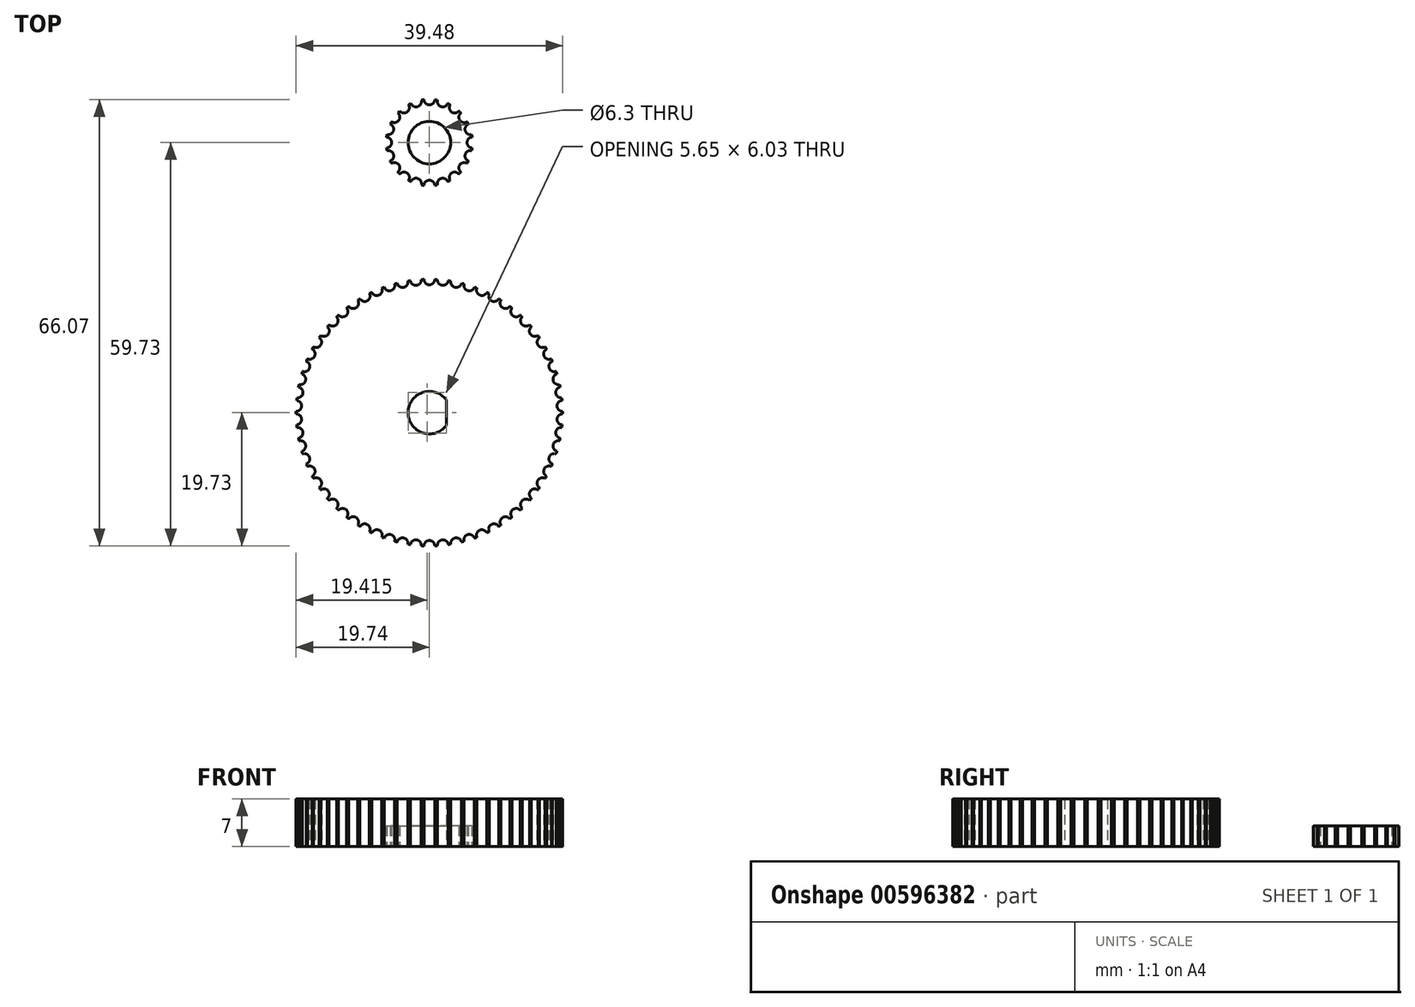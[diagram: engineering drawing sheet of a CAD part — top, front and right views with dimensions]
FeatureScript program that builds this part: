
annotation { "Feature Type Name" : "Feature", "Feature Type Description" : "" }
export const myFeature = defineFeature(function(context is Context, id is Id, definition is map)
    precondition{}
    {
        {
            var Q0;
            Q0=qCreatedBy(makeId("Top.planeOp"),FACE);
            var sketch = newSketch(context, id + "F0", { "sketchPlane" : qUnion([Q0])});
            skCircle(sketch, "E0", {"center": v(0, 0) * mm, "radius": 6.4 * mm});
            skCircle(sketch, "E1", {"center": v(0, 6.4) * mm, "radius": 0.8 * mm});
            skCircle(sketch, "E2.1.0", {"center": v(-1.98, 6.08) * mm, "radius": 0.8 * mm});
            skCircle(sketch, "E2.2.0", {"center": v(-3.76, 5.17) * mm, "radius": 0.8 * mm});
            skCircle(sketch, "E3.1.3.0", {"center": v(-5.17, 3.76) * mm, "radius": 0.8 * mm});
            skCircle(sketch, "E3.1.4.0", {"center": v(-6.08, 1.98) * mm, "radius": 0.8 * mm});
            skCircle(sketch, "E3.1.5.0", {"center": v(-6.4, 0) * mm, "radius": 0.8 * mm});
            skCircle(sketch, "E3.1.6.0", {"center": v(-6.08, -1.98) * mm, "radius": 0.8 * mm});
            skCircle(sketch, "E3.1.7.0", {"center": v(-5.17, -3.76) * mm, "radius": 0.8 * mm});
            skCircle(sketch, "E3.1.8.0", {"center": v(-3.76, -5.17) * mm, "radius": 0.8 * mm});
            skCircle(sketch, "E3.1.9.0", {"center": v(-1.98, -6.08) * mm, "radius": 0.8 * mm});
            skCircle(sketch, "E3.1.10.0", {"center": v(0, -6.4) * mm, "radius": 0.8 * mm});
            skCircle(sketch, "E3.1.11.0", {"center": v(1.98, -6.08) * mm, "radius": 0.8 * mm});
            skCircle(sketch, "E3.1.12.0", {"center": v(3.76, -5.17) * mm, "radius": 0.8 * mm});
            skCircle(sketch, "E3.1.13.0", {"center": v(5.17, -3.76) * mm, "radius": 0.8 * mm});
            skCircle(sketch, "E3.1.14.0", {"center": v(6.08, -1.98) * mm, "radius": 0.8 * mm});
            skCircle(sketch, "E3.1.15.0", {"center": v(6.4, 0) * mm, "radius": 0.8 * mm});
            skCircle(sketch, "E3.1.16.0", {"center": v(6.08, 1.98) * mm, "radius": 0.8 * mm});
            skCircle(sketch, "E3.1.17.0", {"center": v(5.17, 3.76) * mm, "radius": 0.8 * mm});
            skCircle(sketch, "E3.1.18.0", {"center": v(3.76, 5.17) * mm, "radius": 0.8 * mm});
            skCircle(sketch, "E3.1.19.0", {"center": v(1.98, 6.08) * mm, "radius": 0.8 * mm});
            skLineSegment(sketch, "E4", {"start": v(-1.98, 6.08) * mm, "end": v(0, 6.4) * mm, "construction": true});
            skCircle(sketch, "E5", {"center": v(0, 0) * mm, "radius": 3.15 * mm});
            skLineSegment(sketch, "E6", {"start": v(2.5, 1.92) * mm, "end": v(2.5, -1.92) * mm});
            skSolve(sketch);
        }
        {
            var Q0;
            {var subQ1=sQuery(id+"F0.wireOp",EDGE,"E0");var subQ45=sQuery(id+"F0.wireOp",EDGE,"E3.1.16.0");var subQ48=makeQuery(id+"F0.imprint","INTERSECT",VERTEX,{"disambiguationData":[OD(0.0)],"derivedFrom":[subQ1,subQ45]});Q0=makeQuery(id+"F0.imprint","IMPRINT",FACE,{"disambiguationData":[TD([[makeQuery(id+"F0.imprint","IMPRINT",EDGE,{"disambiguationData":[TD([[subQ48,1.0]])],"derivedFrom":subQ1}),1.0]])]});}
            extrude(context, id + "F1", {"entities" : qUnion([Q0]), "depth" : 3 * mm, "offsetDistance" : 25 * mm});
        }
        {
            var Q0;
            Q0=qCreatedBy(makeId("Top.planeOp"),FACE);
            var sketch = newSketch(context, id + "F2", { "sketchPlane" : qUnion([Q0])});
            skCircle(sketch, "E7", {"center": v(0, -40) * mm, "radius": 19.74 * mm});
            skCircle(sketch, "E8", {"center": v(0, -20.26) * mm, "radius": 0.8 * mm});
            skCircle(sketch, "E9.1.0", {"center": v(-2, -20.36) * mm, "radius": 0.8 * mm});
            skCircle(sketch, "E9.2.0", {"center": v(-3.97, -20.66) * mm, "radius": 0.8 * mm});
            skCircle(sketch, "E9.3.0", {"center": v(-5.91, -21.16) * mm, "radius": 0.8 * mm});
            skCircle(sketch, "E9.4.0", {"center": v(-7.79, -21.86) * mm, "radius": 0.8 * mm});
            skCircle(sketch, "E9.5.0", {"center": v(-9.58, -22.74) * mm, "radius": 0.8 * mm});
            skCircle(sketch, "E9.6.0", {"center": v(-11.28, -23.8) * mm, "radius": 0.8 * mm});
            skCircle(sketch, "E9.7.0", {"center": v(-12.86, -25.02) * mm, "radius": 0.8 * mm});
            skCircle(sketch, "E9.8.0", {"center": v(-14.31, -26.4) * mm, "radius": 0.8 * mm});
            skCircle(sketch, "E9.9.0", {"center": v(-15.61, -27.91) * mm, "radius": 0.8 * mm});
            skCircle(sketch, "E9.10.0", {"center": v(-16.76, -29.56) * mm, "radius": 0.8 * mm});
            skCircle(sketch, "E9.11.0", {"center": v(-17.73, -31.3) * mm, "radius": 0.8 * mm});
            skCircle(sketch, "E9.12.0", {"center": v(-18.51, -33.14) * mm, "radius": 0.8 * mm});
            skCircle(sketch, "E9.13.0", {"center": v(-19.11, -35.05) * mm, "radius": 0.8 * mm});
            skCircle(sketch, "E9.14.0", {"center": v(-19.52, -37.01) * mm, "radius": 0.8 * mm});
            skCircle(sketch, "E9.15.0", {"center": v(-19.72, -39) * mm, "radius": 0.8 * mm});
            skCircle(sketch, "E9.16.0", {"center": v(-19.72, -41) * mm, "radius": 0.8 * mm});
            skCircle(sketch, "E9.17.0", {"center": v(-19.52, -42.99) * mm, "radius": 0.8 * mm});
            skCircle(sketch, "E9.18.0", {"center": v(-19.11, -44.95) * mm, "radius": 0.8 * mm});
            skCircle(sketch, "E9.19.0", {"center": v(-18.51, -46.86) * mm, "radius": 0.8 * mm});
            skCircle(sketch, "E9.20.0", {"center": v(-17.73, -48.7) * mm, "radius": 0.8 * mm});
            skCircle(sketch, "E9.21.0", {"center": v(-16.76, -50.44) * mm, "radius": 0.8 * mm});
            skCircle(sketch, "E9.22.0", {"center": v(-15.61, -52.09) * mm, "radius": 0.8 * mm});
            skCircle(sketch, "E9.23.0", {"center": v(-14.31, -53.6) * mm, "radius": 0.8 * mm});
            skCircle(sketch, "E9.24.0", {"center": v(-12.86, -54.98) * mm, "radius": 0.8 * mm});
            skCircle(sketch, "E9.25.0", {"center": v(-11.28, -56.2) * mm, "radius": 0.8 * mm});
            skCircle(sketch, "E9.26.0", {"center": v(-9.58, -57.26) * mm, "radius": 0.8 * mm});
            skCircle(sketch, "E9.27.0", {"center": v(-7.79, -58.14) * mm, "radius": 0.8 * mm});
            skCircle(sketch, "E9.28.0", {"center": v(-5.91, -58.84) * mm, "radius": 0.8 * mm});
            skCircle(sketch, "E9.29.0", {"center": v(-3.97, -59.34) * mm, "radius": 0.8 * mm});
            skCircle(sketch, "E9.30.0", {"center": v(-2, -59.64) * mm, "radius": 0.8 * mm});
            skCircle(sketch, "E9.31.0", {"center": v(0, -59.74) * mm, "radius": 0.8 * mm});
            skCircle(sketch, "E9.32.0", {"center": v(2, -59.64) * mm, "radius": 0.8 * mm});
            skCircle(sketch, "E9.33.0", {"center": v(3.97, -59.34) * mm, "radius": 0.8 * mm});
            skCircle(sketch, "E9.34.0", {"center": v(5.91, -58.84) * mm, "radius": 0.8 * mm});
            skCircle(sketch, "E9.35.0", {"center": v(7.79, -58.14) * mm, "radius": 0.8 * mm});
            skCircle(sketch, "E9.36.0", {"center": v(9.58, -57.26) * mm, "radius": 0.8 * mm});
            skCircle(sketch, "E9.37.0", {"center": v(11.28, -56.2) * mm, "radius": 0.8 * mm});
            skCircle(sketch, "E9.38.0", {"center": v(12.86, -54.98) * mm, "radius": 0.8 * mm});
            skCircle(sketch, "E9.39.0", {"center": v(14.31, -53.6) * mm, "radius": 0.8 * mm});
            skCircle(sketch, "E9.40.0", {"center": v(15.61, -52.09) * mm, "radius": 0.8 * mm});
            skCircle(sketch, "E9.41.0", {"center": v(16.76, -50.44) * mm, "radius": 0.8 * mm});
            skCircle(sketch, "E9.42.0", {"center": v(17.73, -48.7) * mm, "radius": 0.8 * mm});
            skCircle(sketch, "E9.43.0", {"center": v(18.51, -46.86) * mm, "radius": 0.8 * mm});
            skCircle(sketch, "E9.44.0", {"center": v(19.11, -44.95) * mm, "radius": 0.8 * mm});
            skCircle(sketch, "E9.45.0", {"center": v(19.52, -42.99) * mm, "radius": 0.8 * mm});
            skCircle(sketch, "E9.46.0", {"center": v(19.72, -41) * mm, "radius": 0.8 * mm});
            skCircle(sketch, "E9.47.0", {"center": v(19.72, -39) * mm, "radius": 0.8 * mm});
            skCircle(sketch, "E9.48.0", {"center": v(19.52, -37.01) * mm, "radius": 0.8 * mm});
            skCircle(sketch, "E9.49.0", {"center": v(19.11, -35.05) * mm, "radius": 0.8 * mm});
            skCircle(sketch, "E9.50.0", {"center": v(18.51, -33.14) * mm, "radius": 0.8 * mm});
            skCircle(sketch, "E9.51.0", {"center": v(17.73, -31.3) * mm, "radius": 0.8 * mm});
            skCircle(sketch, "E9.52.0", {"center": v(16.76, -29.56) * mm, "radius": 0.8 * mm});
            skCircle(sketch, "E9.53.0", {"center": v(15.61, -27.91) * mm, "radius": 0.8 * mm});
            skCircle(sketch, "E9.54.0", {"center": v(14.31, -26.4) * mm, "radius": 0.8 * mm});
            skCircle(sketch, "E9.55.0", {"center": v(12.86, -25.02) * mm, "radius": 0.8 * mm});
            skCircle(sketch, "E9.56.0", {"center": v(11.28, -23.8) * mm, "radius": 0.8 * mm});
            skCircle(sketch, "E9.57.0", {"center": v(9.58, -22.74) * mm, "radius": 0.8 * mm});
            skCircle(sketch, "E9.58.0", {"center": v(7.79, -21.86) * mm, "radius": 0.8 * mm});
            skCircle(sketch, "E9.59.0", {"center": v(5.91, -21.16) * mm, "radius": 0.8 * mm});
            skCircle(sketch, "E9.60.0", {"center": v(3.97, -20.66) * mm, "radius": 0.8 * mm});
            skCircle(sketch, "E9.61.0", {"center": v(2, -20.36) * mm, "radius": 0.8 * mm});
            skLineSegment(sketch, "E10", {"start": v(0, -20.26) * mm, "end": v(2, -20.36) * mm, "construction": true});
            skCircle(sketch, "E11", {"center": v(0, -40) * mm, "radius": 3.15 * mm});
            skLineSegment(sketch, "E12", {"start": v(2.5, -38.08) * mm, "end": v(2.5, -41.92) * mm});
            skSolve(sketch);
        }
        {
            var Q0;
            {var subQ0=sQuery(id+"F2.wireOp",EDGE,"E9.47.0");var subQ1=sQuery(id+"F2.wireOp",EDGE,"E7");var subQ119=makeQuery(id+"F2.imprint","INTERSECT",VERTEX,{"disambiguationData":[OD(0.0)],"derivedFrom":[subQ1,subQ0]});Q0=makeQuery(id+"F2.imprint","IMPRINT",FACE,{"disambiguationData":[TD([[makeQuery(id+"F2.imprint","IMPRINT",EDGE,{"disambiguationData":[TD([[subQ119,-1.0]])],"derivedFrom":subQ1}),1.0]])]});}
            var Q1;
            {var subQ0=sQuery(id+"F2.wireOp",EDGE,"E12");Q1=makeQuery(id+"F2.imprint","IMPRINT",FACE,{"disambiguationData":[TD([[makeQuery(id+"F2.imprint","IMPRINT",EDGE,{"derivedFrom":subQ0}),1.0]])]});}
            extrude(context, id + "F3", {"entities" : qUnion([Q0, Q1]), "depth" : 7 * mm, "offsetDistance" : 25 * mm});
        }
    });
